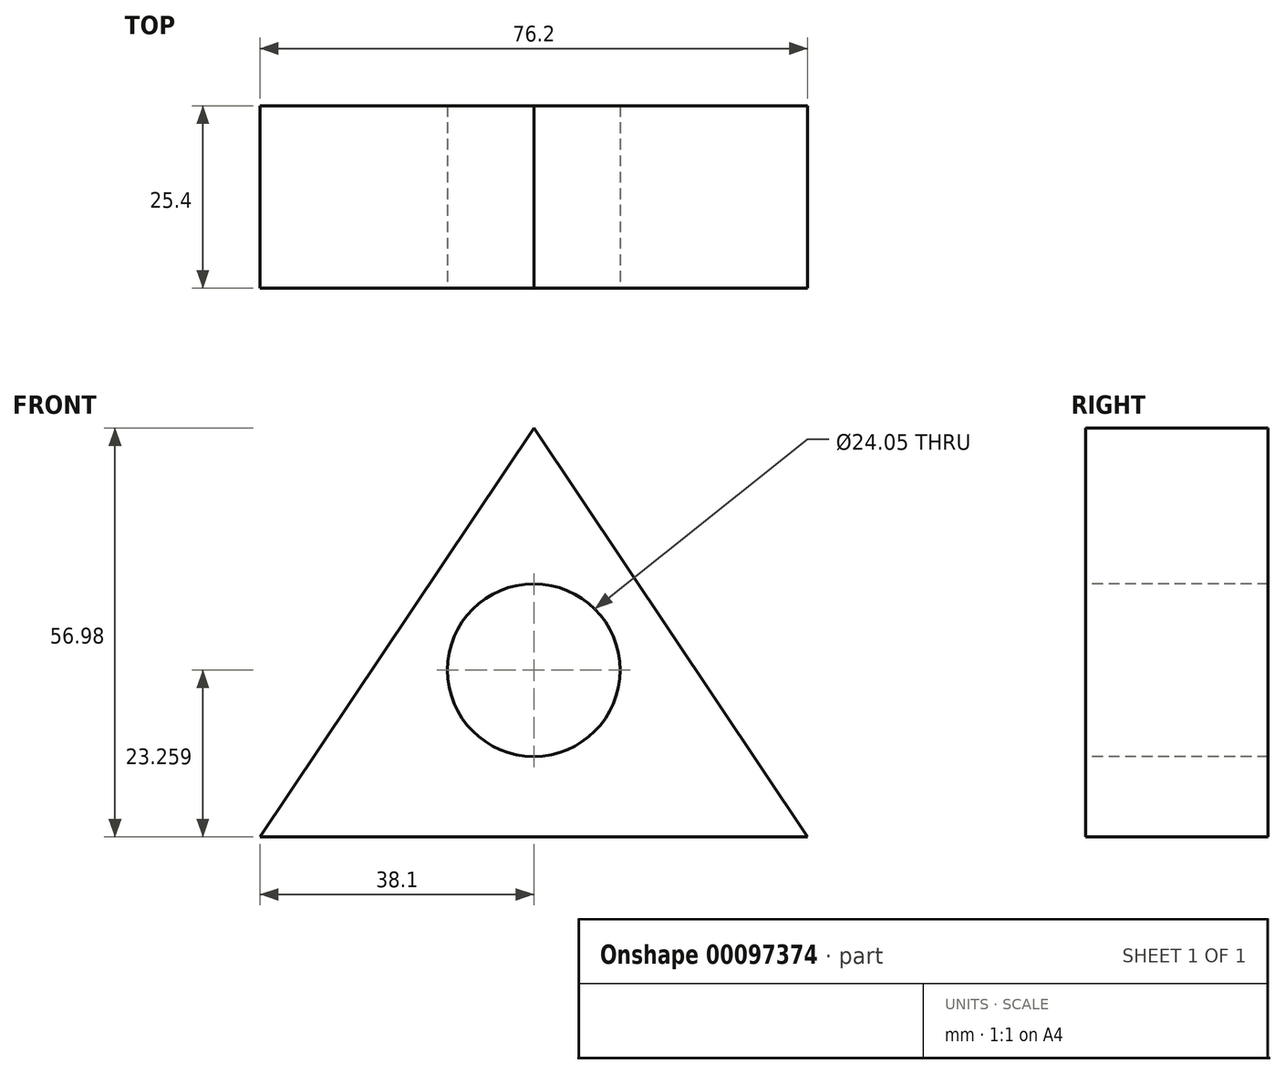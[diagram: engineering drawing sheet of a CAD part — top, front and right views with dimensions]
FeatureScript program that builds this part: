
annotation { "Feature Type Name" : "Feature", "Feature Type Description" : "" }
export const myFeature = defineFeature(function(context is Context, id is Id, definition is map)
    precondition{}
    {
        {
            var Q0;
            Q0=qCreatedBy(makeId("Front.planeOp"),FACE);
            var sketch = newSketch(context, id + "F0", { "sketchPlane" : qUnion([Q0])});
            skLineSegment(sketch, "E0", {"start": v(0, 0) * mm, "end": v(76.2, 0) * mm});
            skLineSegment(sketch, "E1", {"start": v(0, 0) * mm, "end": v(38.1, 56.98) * mm});
            skLineSegment(sketch, "E2", {"start": v(38.1, 56.98) * mm, "end": v(76.2, 0) * mm});
            skPoint(sketch, "E3", {"position": v(38.1, 0) * mm});
            skSolve(sketch);
        }
        {
            var Q0;
            Q0=makeQuery(id+"F0.imprint","IMPRINT",FACE,{"disambiguationData":[TD([[makeQuery(id+"F0.imprint","IMPRINT",EDGE,{"derivedFrom":sQuery(id+"F0.wireOp",EDGE,"E0")}),1.0]])]});
            extrude(context, id + "F1", {"entities" : qUnion([Q0]), "depth" : 25.4 * mm});
        }
        {
            var Q0;
            Q0=makeQuery(id+"F1.opExtrude","CAP_FACE",FACE,{"disambiguationData":[OSD([sQuery(id+"F0.wireOp",EDGE,"E0"),sQuery(id+"F0.wireOp",EDGE,"E1"),sQuery(id+"F0.wireOp",EDGE,"E2")])],"isStart":false});
            var sketch = newSketch(context, id + "F2", { "sketchPlane" : qUnion([Q0])});
            skLineSegment(sketch, "E4", {"start": v(38.1, 23.26) * mm, "end": v(38.1, 0) * mm});
            skPoint(sketch, "E4.startSnap0", {"position": v(38.1, 0) * mm});
            skCircle(sketch, "E5", {"center": v(38.1, 23.26) * mm, "radius": 12.03 * mm});
            skSolve(sketch);
        }
        {
            var Q0;
            Q0=makeQuery(id+"F2.imprint","IMPRINT",FACE,{"disambiguationData":[TD([[makeQuery(id+"F2.imprint","IMPRINT",EDGE,{"derivedFrom":sQuery(id+"F2.wireOp",EDGE,"E5")}),1.0]])]});
            extrude(context, id + "F3", {"entities" : qUnion([Q0]), "operationType" : NewBodyOperationType.REMOVE, "oppositeDirection" : true, "depth" : 25.4 * mm});
        }
    });
